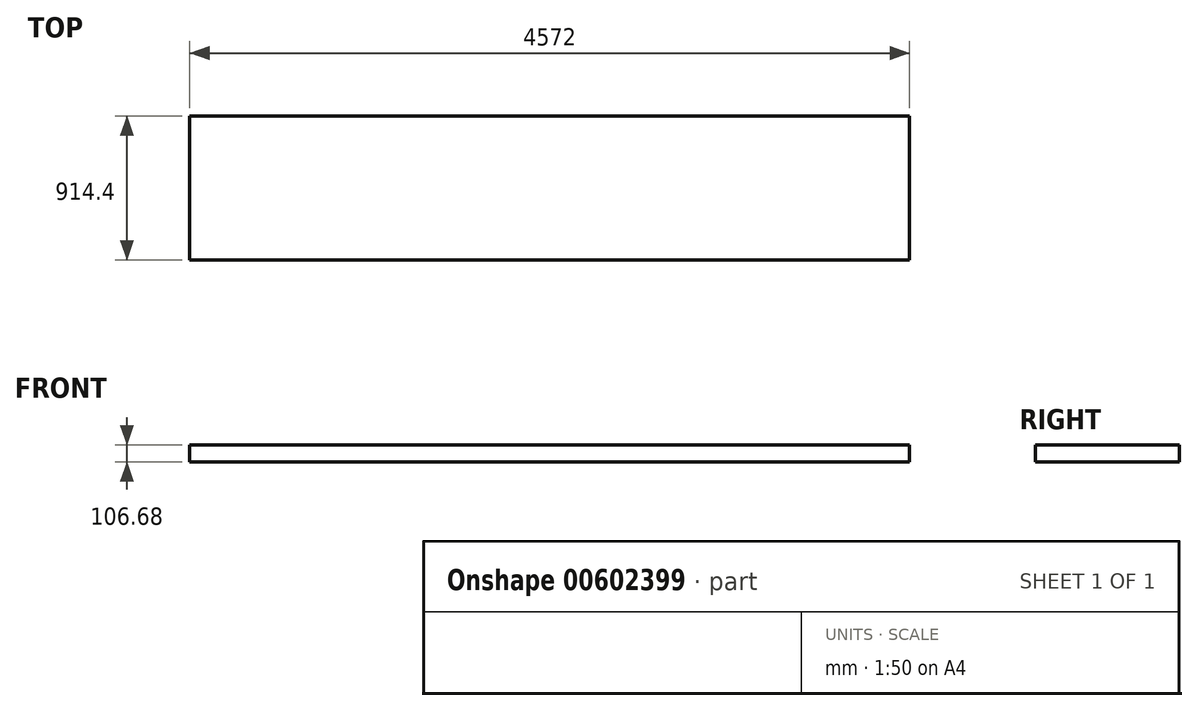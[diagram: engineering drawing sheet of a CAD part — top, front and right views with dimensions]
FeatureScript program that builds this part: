
annotation { "Feature Type Name" : "Feature", "Feature Type Description" : "" }
export const myFeature = defineFeature(function(context is Context, id is Id, definition is map)
    precondition{}
    {
        {
            var Q0;
            Q0=qCreatedBy(makeId("Top.planeOp"),FACE);
            var sketch = newSketch(context, id + "F0", { "sketchPlane" : qUnion([Q0])});
            skLineSegment(sketch, "E0.bottom", {"start": v(0, 0) * mm, "end": v(4572, 0) * mm});
            skLineSegment(sketch, "E0.top", {"start": v(0, -914.4) * mm, "end": v(4572, -914.4) * mm});
            skLineSegment(sketch, "E0.left", {"start": v(0, 0) * mm, "end": v(0, -914.4) * mm});
            skLineSegment(sketch, "E0.right", {"start": v(4572, 0) * mm, "end": v(4572, -914.4) * mm});
            skSolve(sketch);
        }
        {
            var Q0;
            Q0=makeQuery(id+"F0.imprint","IMPRINT",FACE,{"disambiguationData":[TD([[makeQuery(id+"F0.imprint","IMPRINT",EDGE,{"derivedFrom":sQuery(id+"F0.wireOp",EDGE,"E0.bottom")}),-1.0]])]});
            extrude(context, id + "F1", {"entities" : qUnion([Q0]), "depth" : 106.68 * mm, "offsetDistance" : 30.48 * mm});
        }
    });
